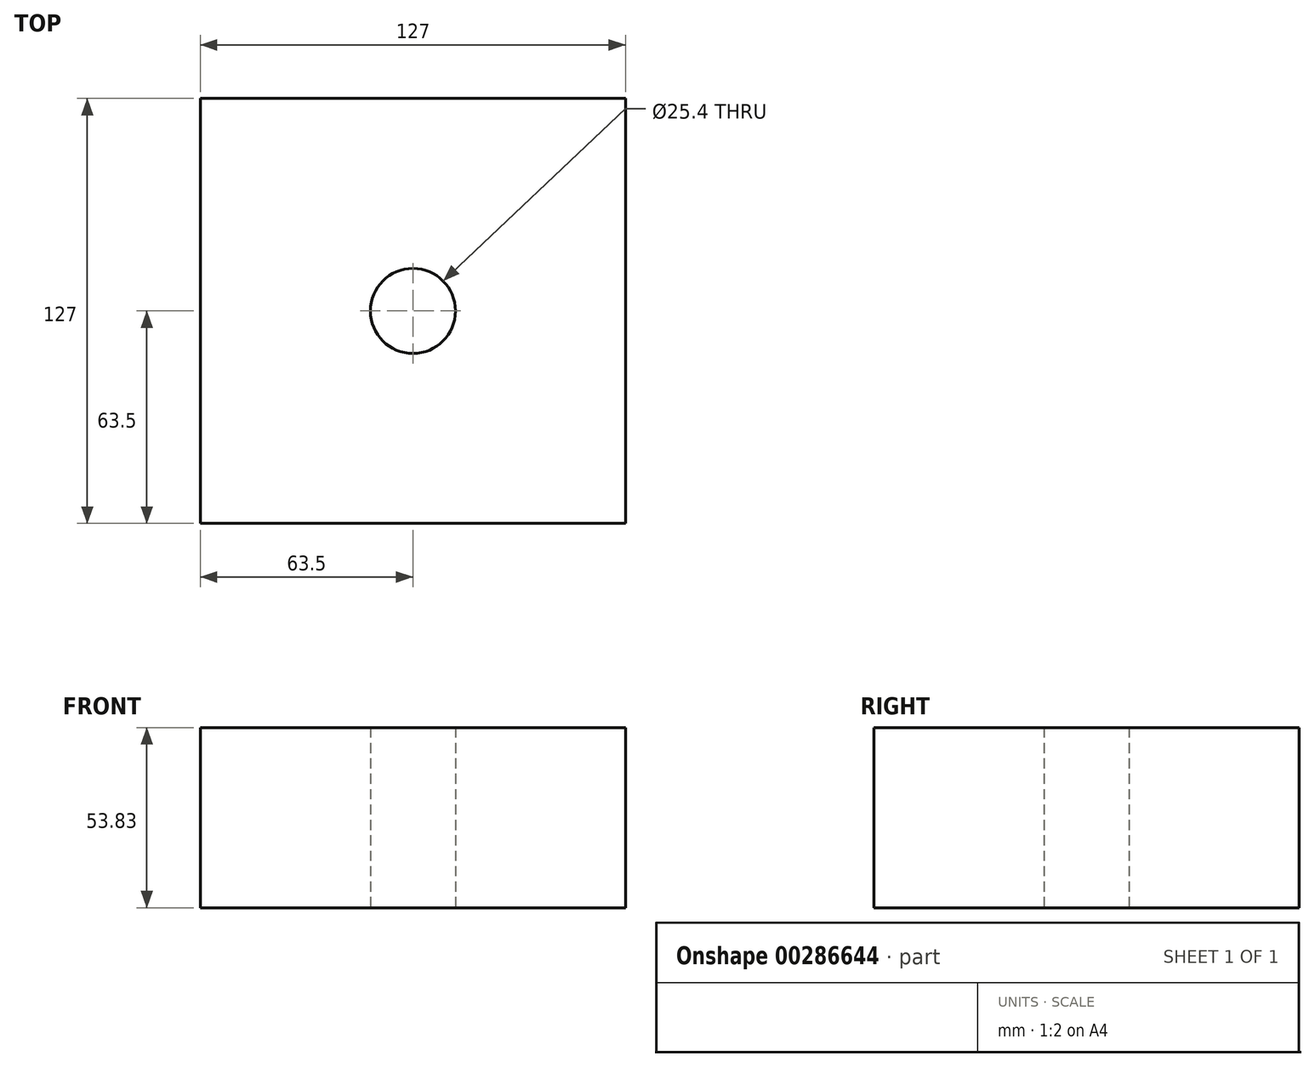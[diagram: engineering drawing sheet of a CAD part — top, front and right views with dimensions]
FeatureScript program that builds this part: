
annotation { "Feature Type Name" : "Feature", "Feature Type Description" : "" }
export const myFeature = defineFeature(function(context is Context, id is Id, definition is map)
    precondition{}
    {
        {
            var Q0;
            Q0=qCreatedBy(makeId("Top.planeOp"),FACE);
            var sketch = newSketch(context, id + "F0", { "sketchPlane" : qUnion([Q0])});
            skCircle(sketch, "E0", {"center": v(0, 0) * mm, "radius": 12.7 * mm});
            skSolve(sketch);
        }
        {
            var Q0;
            Q0 = qSketchRegion(id + "F0", true);
            extrude(context, id + "F1", {"entities" : qUnion([Q0]), "depth" : 152.4 * mm});
        }
        {
            var Q0;
            Q0=qCreatedBy(makeId("Top.planeOp"),FACE);
            var sketch = newSketch(context, id + "F2", { "sketchPlane" : qUnion([Q0])});
            skLineSegment(sketch, "E1.bottom", {"start": v(63.5, -63.5) * mm, "end": v(-63.5, -63.5) * mm});
            skLineSegment(sketch, "E1.top", {"start": v(63.5, 63.5) * mm, "end": v(-63.5, 63.5) * mm});
            skLineSegment(sketch, "E1.left", {"start": v(63.5, -63.5) * mm, "end": v(63.5, 63.5) * mm});
            skLineSegment(sketch, "E1.right", {"start": v(-63.5, -63.5) * mm, "end": v(-63.5, 63.5) * mm});
            skPoint(sketch, "E1.middle", {"position": v(0, 0) * mm});
            skSolve(sketch);
        }
        {
            var Q0;
            Q0 = qSketchRegion(id + "F2", true);
            extrude(context, id + "F3", {"entities" : qUnion([Q0]), "depth" : 53.83 * mm});
        }
        {
            var Q0;
            Q0=makeQuery(id+"F1.opExtrude","SWEPT_BODY",BODY,{"disambiguationData":[OSD([sQuery(id+"F0.wireOp",EDGE,"E0")])]});
            var Q1;
            Q1=makeQuery(id+"F3.opExtrude","SWEPT_BODY",BODY,{"disambiguationData":[OSD([sQuery(id+"F2.wireOp",EDGE,"E1.bottom"),sQuery(id+"F2.wireOp",EDGE,"E1.top"),sQuery(id+"F2.wireOp",EDGE,"E1.left"),sQuery(id+"F2.wireOp",EDGE,"E1.right")])]});
            booleanBodies(context, id + "F4", {"operationType" : BooleanOperationType.SUBTRACTION, "tools" : qUnion([Q0]), "targets" : qUnion([Q1])});
        }
    });
